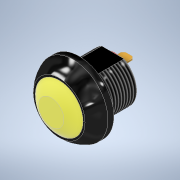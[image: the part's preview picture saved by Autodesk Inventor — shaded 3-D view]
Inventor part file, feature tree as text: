
AUTODESK INVENTOR PART (.ipt)
format: ipt  version: 2021 (Build 250183000, 183)  size: 201,216 bytes
history: native  units: mm
features: sketch x3, extrude x2, revolve x1, chamfer x1, thread x1
ambient origin geometry x8: Origin, YZ Plane, XZ Plane, XY Plane, X Axis, Y Axis, Z Axis, Center Point
bodies: Solid1 (feature_tree)
feature tree (8):
  revolve  "Revolution1"  [1 undecoded]
  extrude  "Extrusion1"  Depth=5.0mm
  chamfer  "Chamfer1"  Distance=6.4mm
  thread  "Thread1"  [1 undecoded]
  extrude  "Extrusion2"  Depth=3.5mm
  sketch  "Sketch1"  dims[d0=17.5mm d1=1.5mm]
  sketch  "Sketch2"  dims[d2=13.0mm d3=5.0mm]
  sketch  "Sketch3"  dims[d4=2.0mm d5=6.4mm d6=12.0mm d7=12.0mm d8=8.5mm d9=10.0mm d10=0.5mm d11=90.0deg d12=2.8mm d13=0.4mm d14=2.8mm d15=0.4mm d16=5.08mm d17=2.54mm d18=3.5mm d19=0.0mm d20=0.5mm d21=2.0mm d22=45.0deg d23=12.5mm d24=0.0mm d25=10.6mm d26=3.5mm d27=0.0mm]
note: 2 required parameter values undecoded (feature->parameter linkage not recoverable at this tier; creation-order binding heuristic only, values carry confidence <= 0.55)